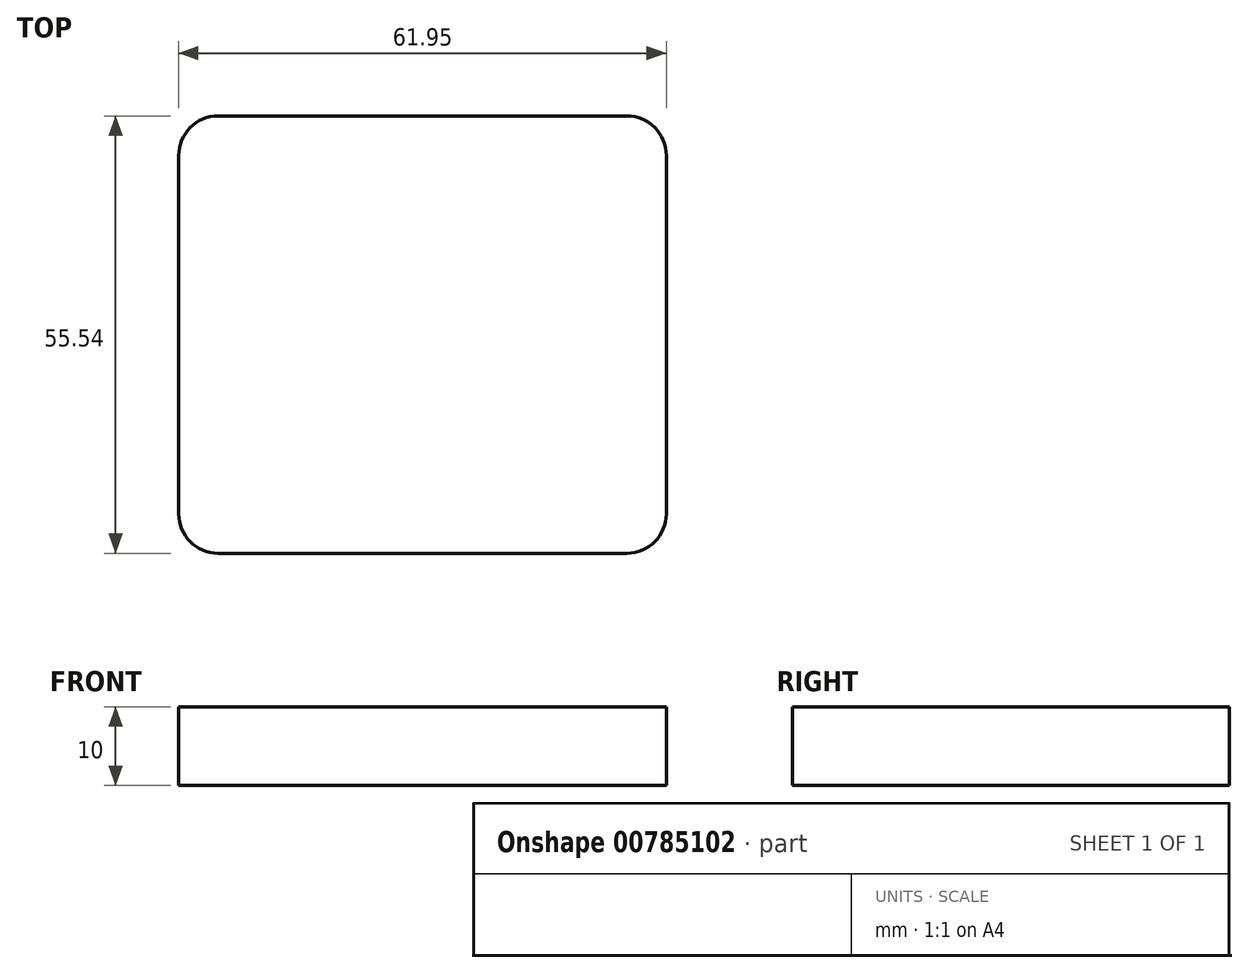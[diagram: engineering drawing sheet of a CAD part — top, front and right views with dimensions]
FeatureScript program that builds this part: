
annotation { "Feature Type Name" : "Feature", "Feature Type Description" : "" }
export const myFeature = defineFeature(function(context is Context, id is Id, definition is map)
    precondition{}
    {
        {
            var Q0;
            Q0=qCreatedBy(makeId("Top.planeOp"),FACE);
            var sketch = newSketch(context, id + "F0", { "sketchPlane" : qUnion([Q0])});
            skLineSegment(sketch, "E0.bottom", {"start": v(5, 0) * mm, "end": v(56.95, 0) * mm});
            skLineSegment(sketch, "E0.top", {"start": v(5, -55.54) * mm, "end": v(56.95, -55.54) * mm});
            skLineSegment(sketch, "E0.left", {"start": v(0, -5) * mm, "end": v(0, -50.54) * mm});
            skLineSegment(sketch, "E0.right", {"start": v(61.95, -5) * mm, "end": v(61.95, -50.54) * mm});
            skPoint(sketch, "E1.visualSharp", {"position": v(0, 0) * mm});
            skArc(sketch, "E1.filletArc", {"start": v(5, 0) * mm, "mid": v(1.46, -1.46) * mm, "end": v(0, -5) * mm});
            skPoint(sketch, "E2.visualSharp", {"position": v(0, -55.54) * mm});
            skArc(sketch, "E2.filletArc", {"start": v(0, -50.54) * mm, "mid": v(1.46, -54.07) * mm, "end": v(5, -55.54) * mm});
            skPoint(sketch, "E3.visualSharp", {"position": v(61.95, 0) * mm});
            skArc(sketch, "E3.filletArc", {"start": v(61.95, -5) * mm, "mid": v(60.48, -1.46) * mm, "end": v(56.95, 0) * mm});
            skPoint(sketch, "E4.visualSharp", {"position": v(61.95, -55.54) * mm});
            skArc(sketch, "E4.filletArc", {"start": v(56.95, -55.54) * mm, "mid": v(60.48, -54.07) * mm, "end": v(61.95, -50.54) * mm});
            skSolve(sketch);
        }
        {
            var Q0;
            Q0 = qSketchRegion(id + "F0", true);
            extrude(context, id + "F1", {"entities" : qUnion([Q0]), "depth" : 10 * mm, "offsetDistance" : 25 * mm});
        }
    });
